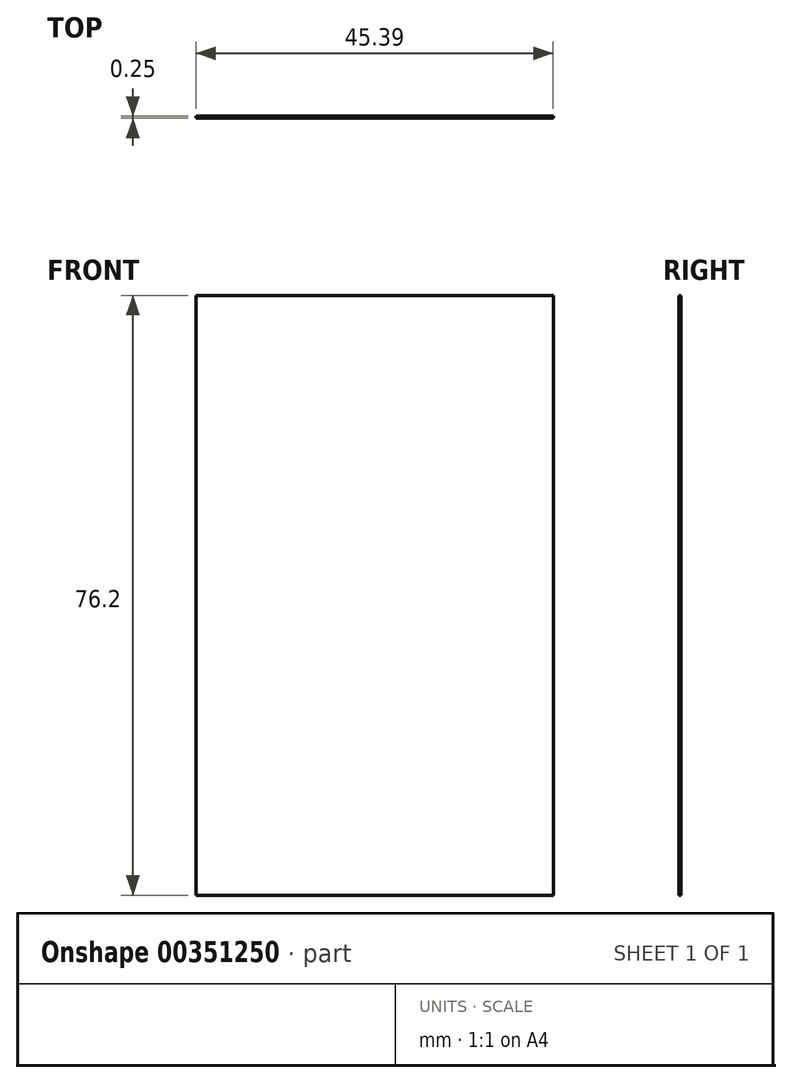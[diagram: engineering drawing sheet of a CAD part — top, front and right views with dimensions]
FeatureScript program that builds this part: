
annotation { "Feature Type Name" : "Feature", "Feature Type Description" : "" }
export const myFeature = defineFeature(function(context is Context, id is Id, definition is map)
    precondition{}
    {
        {
            var Q0;
            Q0=qCreatedBy(makeId("Front.planeOp"),FACE);
            var sketch = newSketch(context, id + "F0", { "sketchPlane" : qUnion([Q0])});
            skLineSegment(sketch, "E0.bottom", {"start": v(-24.3, 26.9) * mm, "end": v(21.1, 26.9) * mm});
            skLineSegment(sketch, "E0.top", {"start": v(-24.3, -49.3) * mm, "end": v(21.1, -49.3) * mm});
            skLineSegment(sketch, "E0.left", {"start": v(-24.3, 26.9) * mm, "end": v(-24.3, -49.3) * mm});
            skLineSegment(sketch, "E0.right", {"start": v(21.1, 26.9) * mm, "end": v(21.1, -49.3) * mm});
            skSolve(sketch);
        }
        {
            var Q0;
            Q0=makeQuery(id+"F0.imprint","IMPRINT",FACE,{"disambiguationData":[TD([[makeQuery(id+"F0.imprint","IMPRINT",EDGE,{"derivedFrom":sQuery(id+"F0.wireOp",EDGE,"E0.bottom")}),-1.0]])]});
            extrude(context, id + "F1", {"entities" : qUnion([Q0]), "depth" : 0.25 * mm});
        }
    });
